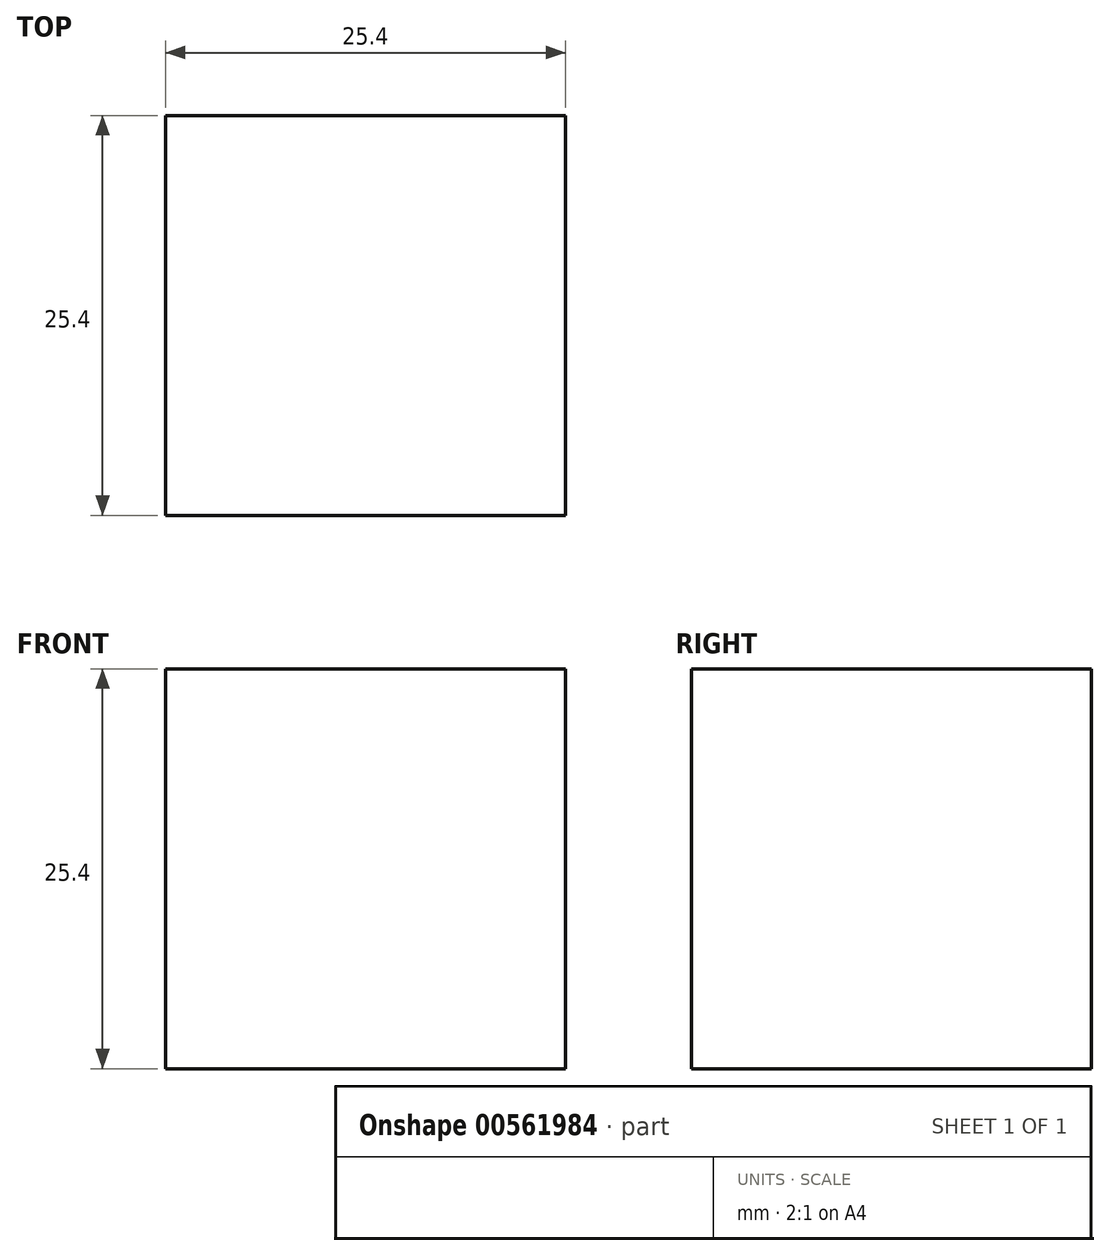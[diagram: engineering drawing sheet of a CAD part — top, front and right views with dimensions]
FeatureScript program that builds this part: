
annotation { "Feature Type Name" : "Feature", "Feature Type Description" : "" }
export const myFeature = defineFeature(function(context is Context, id is Id, definition is map)
    precondition{}
    {
        {
            var Q0;
            Q0=qCreatedBy(makeId("Front.planeOp"),FACE);
            var sketch = newSketch(context, id + "F0", { "sketchPlane" : qUnion([Q0])});
            skLineSegment(sketch, "E0.bottom", {"start": v(-25.4, 42.43) * mm, "end": v(0, 42.43) * mm});
            skLineSegment(sketch, "E0.top", {"start": v(-25.4, 17.03) * mm, "end": v(0, 17.03) * mm});
            skLineSegment(sketch, "E0.left", {"start": v(-25.4, 42.43) * mm, "end": v(-25.4, 17.03) * mm});
            skLineSegment(sketch, "E0.right", {"start": v(0, 42.43) * mm, "end": v(0, 17.03) * mm});
            skSolve(sketch);
        }
        {
            var Q0;
            Q0=makeQuery(id+"F0.imprint","IMPRINT",FACE,{"disambiguationData":[TD([[makeQuery(id+"F0.imprint","IMPRINT",EDGE,{"derivedFrom":sQuery(id+"F0.wireOp",EDGE,"E0.bottom")}),-1.0]])]});
            extrude(context, id + "F1", {"entities" : qUnion([Q0]), "depth" : 25.4 * mm, "offsetDistance" : 25.4 * mm});
        }
    });
